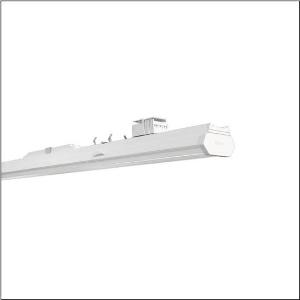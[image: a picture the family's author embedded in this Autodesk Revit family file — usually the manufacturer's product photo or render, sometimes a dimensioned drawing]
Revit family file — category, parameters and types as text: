
# Revit family: licross_11_protected_mo_51tp11cn58xf
name_source: partatom
category: Lighting Fixtures
units: mm (PartAtom-declared; Revit-internal decimal feet)

## family parameters
Cut with Voids When Loaded = No
Host = Face
Light Source = No
Part Type = Normal
Room Calculation Point = No
Round Connector Dimension = Use Diameter
Shared = No

## types (1)
- --- (1 x LED, 8150 lm, 49 W, 5000K)
    Apparent Load = 49 VA
    CIE Flux Codes = 83 94 98 100 100
    Color Rendering = 80
    Color Temperature = 5000K
    Default Elevation = 1800 mm
    Description = Licross 11 Protected MO, luminaire insert, of sheet steel, galvanised, coil coated, white, length: 1.500mm, width: 90mm, height: 101mm, LED rated luminous flux: 8.150lm, light colour: 850, SDCM (Standard Deviation of Colour Matching)MacAdam ≤ 3 SDCM (initial), control gear: ON/OFF Multilumen, CLOi, control gear: ECG Multilumen, with plug, 3-pole, with phase selection, mains connection: 220..240V, AC, 50/60Hz, start of lifetime: 49W, end of service life: 54W, internal wiring halogen-free, primary optical cover: cover, of PMMA, light emission: direct distribution, primary light characteristic: symmetric, protection rating (complete): IP64, insulation class (complete): insulation class I (protective earthing), certification: CE, ENEC, VDE, UKCA, protection symbol: D if used in an environment with conductive dust loads with corresponding accessories, impact resistance: IK06, permissible ambient temperature for indoor applications: -35..+40°C, corresponds to IFS (International Featured Standards) requirements for safety and quality in the food industry, reducing of maximum allowable ambient temperature of 5°C with ceiling mounting, LABS conformity tested according to VDMA 24364:2018-05, The light source and the operating device comply with the requirements of the Ecodesign Regulation (EU) 2019/2020 and are replaceable in accordance with this regulation, packaging unit: 1 piece
    Height = 92 mm
    Lamp = 1 x LED
    Lamp Light Flux = 8150 lm
    Lamp Power = 49 W
    Lamp count = 1
    Length = 1500 mm
    Luminous efficacy = 166 lm/W
    Manufacturer = Siteco
    ModVariant = No
    Model = 51TP11CN58XF
    Mounting Place = Ceiling
    Mounting Type = Pendant
    Number of Poles = 1
    OnlyDefault = Yes
    Power Factor = 1
    Product Name = Licross 11 Protected MO
    Product group = luminaire insert | ceiling pendant
    ProductGroupID = 901
    Protection Class = Protection class I
    Protection Degree = IP 64
    RLX_Detail_Level = 1
    RLX_Emergency_Light_Flux = 0 lm
    RLX_Emergency_Type = 0
    RLX_Emergency_Type_DB = No
    RlxData = <blob elided: 22153 chars, md5=1d9198dd>
    Socket = socket
    Standby Power = 0 W
    System Light Flux = 8150 lm
    System Power = 49 W
    Type Comments = factory setting: luminous flux: 100 % | (A | C | E) | 111 mA
    Type Image = l_1256148.jpg
    URL = http://relux.com
    VarID = @adj_197535
    Voltage = 0 V
    Weight = 0.00 kg
    Width = 88 mm

## geometry (parser evidence)
native form markers: Blend x4, Sweep x9
no freeform markers — native parametric forms only
